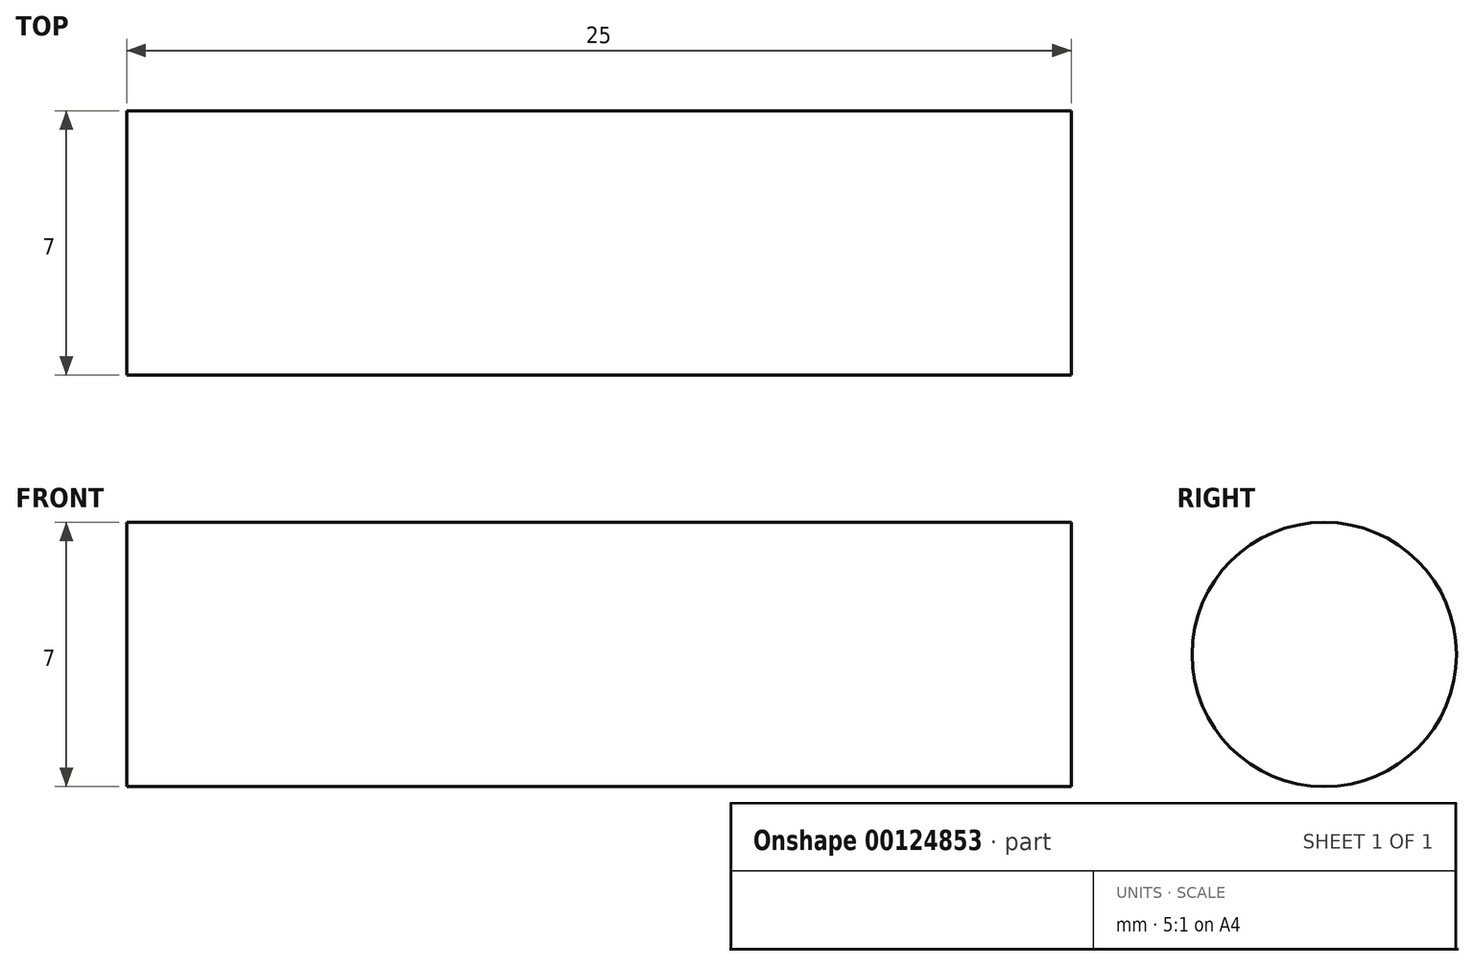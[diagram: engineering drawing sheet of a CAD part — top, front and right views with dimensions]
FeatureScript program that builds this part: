
annotation { "Feature Type Name" : "Feature", "Feature Type Description" : "" }
export const myFeature = defineFeature(function(context is Context, id is Id, definition is map)
    precondition{}
    {
        {
            var Q0;
            Q0=qCreatedBy(makeId("Right.planeOp"),FACE);
            var sketch = newSketch(context, id + "F0", { "sketchPlane" : qUnion([Q0])});
            skCircle(sketch, "E0", {"center": v(0, 0) * mm, "radius": 3.5 * mm});
            skSolve(sketch);
        }
        {
            var Q0;
            Q0 = qSketchRegion(id + "F0", true);
            extrude(context, id + "F1", {"entities" : qUnion([Q0]), "oppositeDirection" : true, "depth" : 25 * mm});
        }
    });
